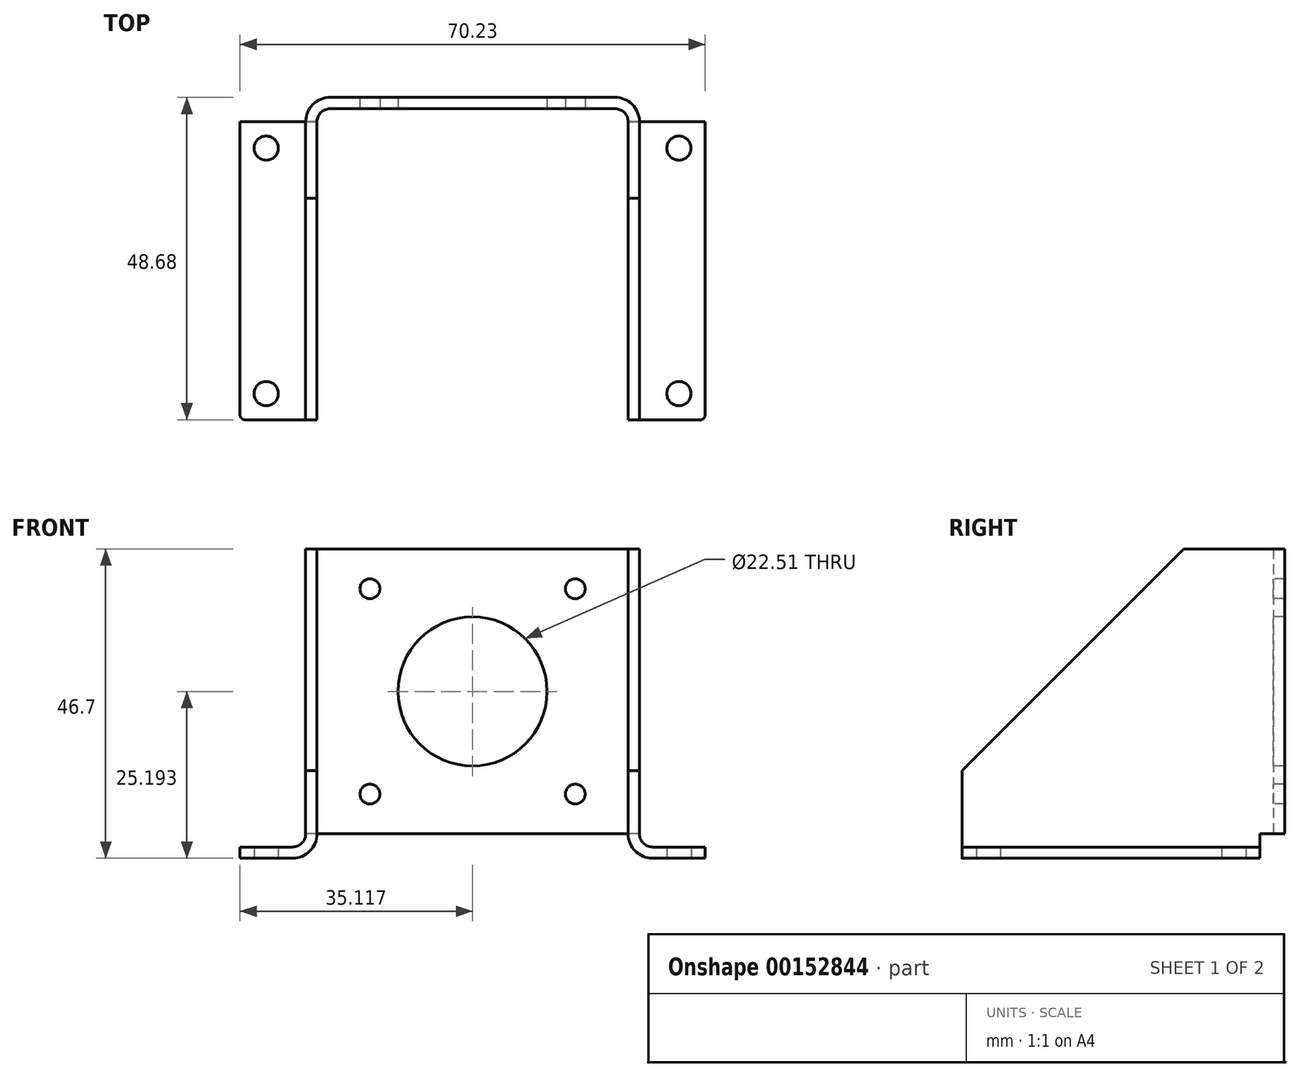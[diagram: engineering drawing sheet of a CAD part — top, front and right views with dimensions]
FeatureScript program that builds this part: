
annotation { "Feature Type Name" : "Feature", "Feature Type Description" : "" }
export const myFeature = defineFeature(function(context is Context, id is Id, definition is map)
    precondition{}
    {
        {
            var Q0;
            Q0=qCreatedBy(makeId("Top.planeOp"),FACE);
            var sketch = newSketch(context, id + "F0", { "sketchPlane" : qUnion([Q0])});
            skLineSegment(sketch, "E0.bottom", {"start": v(0, 0) * mm, "end": v(-1.7, 0) * mm});
            skLineSegment(sketch, "E1.left", {"start": v(0, 0) * mm, "end": v(0, 46.97) * mm});
            skLineSegment(sketch, "E1.right", {"start": v(-1.7, 0) * mm, "end": v(-1.7, 48.68) * mm});
            skLineSegment(sketch, "E2.bottom", {"start": v(0, 46.97) * mm, "end": v(46.97, 46.97) * mm});
            skLineSegment(sketch, "E2.top", {"start": v(-1.7, 48.68) * mm, "end": v(48.68, 48.68) * mm});
            skLineSegment(sketch, "E3.top", {"start": v(46.97, 0) * mm, "end": v(48.68, 0) * mm});
            skLineSegment(sketch, "E3.left", {"start": v(46.97, 46.97) * mm, "end": v(46.97, 0) * mm});
            skLineSegment(sketch, "E3.right", {"start": v(48.68, 48.68) * mm, "end": v(48.68, 0) * mm});
            skLineSegment(sketch, "E4", {"start": v(0, 46.97) * mm, "end": v(-1.7, 46.97) * mm, "construction": true});
            skLineSegment(sketch, "E5", {"start": v(0, 46.97) * mm, "end": v(0, 48.68) * mm, "construction": true});
            skLineSegment(sketch, "E6", {"start": v(46.97, 46.97) * mm, "end": v(48.68, 46.97) * mm, "construction": true});
            skLineSegment(sketch, "E7", {"start": v(46.97, 46.97) * mm, "end": v(46.97, 48.68) * mm, "construction": true});
            skSolve(sketch);
        }
        {
            var Q0;
            Q0=qSketchRegion(id+"F0",true);
            extrude(context, id + "F1", {"entities" : qUnion([Q0]), "depth" : 43 * mm});
        }
        {
            var Q0;
            Q0=makeQuery(id+"F1.opExtrude","SWEPT_FACE",FACE,{"disambiguationData":[OSD([sQuery(id+"F0.wireOp",EDGE,"E2.bottom")])]});
            cPlane(context, id + "F2", {"entities" : qUnion([Q0]), "cplaneType" : CPlaneType.OFFSET, "offset" : 1.98 * mm, "width" : 152.4 * mm, "height" : 152.4 * mm});
        }
        {
            var Q0;
            Q0=makeQuery(id+"F1.opExtrude","SWEPT_FACE",FACE,{"disambiguationData":[OSD([sQuery(id+"F0.wireOp",EDGE,"E3.top")])]});
            var sketch = newSketch(context, id + "F3", { "sketchPlane" : qUnion([Q0])});
            skLineSegment(sketch, "E8.bottom", {"start": v(46.97, 0) * mm, "end": v(48.68, 0) * mm});
            skLineSegment(sketch, "E8.left", {"start": v(46.97, 0) * mm, "end": v(46.97, -3.7) * mm});
            skLineSegment(sketch, "E8.right", {"start": v(48.68, 0) * mm, "end": v(48.68, -1.98) * mm});
            skLineSegment(sketch, "E9.bottom", {"start": v(48.68, -1.98) * mm, "end": v(58.6, -1.98) * mm});
            skLineSegment(sketch, "E9.top", {"start": v(46.97, -3.7) * mm, "end": v(58.6, -3.7) * mm});
            skLineSegment(sketch, "E9.right", {"start": v(58.6, -1.98) * mm, "end": v(58.6, -3.7) * mm});
            skLineSegment(sketch, "E10.bottom", {"start": v(-1.7, 0) * mm, "end": v(0, 0) * mm});
            skLineSegment(sketch, "E10.left", {"start": v(-1.7, 0) * mm, "end": v(-1.7, -1.98) * mm});
            skLineSegment(sketch, "E10.right", {"start": v(0, 0) * mm, "end": v(0, -3.7) * mm});
            skLineSegment(sketch, "E11.bottom", {"start": v(-1.7, -1.98) * mm, "end": v(-11.63, -1.98) * mm});
            skLineSegment(sketch, "E11.top", {"start": v(0, -3.7) * mm, "end": v(-11.63, -3.7) * mm});
            skLineSegment(sketch, "E11.right", {"start": v(-11.63, -1.98) * mm, "end": v(-11.63, -3.7) * mm});
            skSolve(sketch);
        }
        {
            var Q0;
            Q0=makeQuery(id+"F3.imprint","IMPRINT",FACE,{"disambiguationData":[TD([[makeQuery(id+"F3.imprint","IMPRINT",EDGE,{"derivedFrom":sQuery(id+"F3.wireOp",EDGE,"E8.bottom")}),-1.0]])]});
            var Q1;
            Q1=makeQuery(id+"F3.imprint","IMPRINT",FACE,{"disambiguationData":[TD([[makeQuery(id+"F3.imprint","IMPRINT",EDGE,{"derivedFrom":sQuery(id+"F3.wireOp",EDGE,"E10.bottom")}),-1.0]])]});
            var Q2;
            Q2=qCreatedBy(id+"F2.planeOp",FACE);
            extrude(context, id + "F4", {"entities" : qUnion([Q0, Q1]), "operationType" : NewBodyOperationType.ADD, "endBound" : BoundingType.UP_TO_SURFACE, "oppositeDirection" : true, "endBoundEntityFace" : qUnion([Q2]), "depth" : 25.4 * mm});
        }
        {
            var Q0;
            Q0=makeQuery(id+"F1.opExtrude","SWEPT_EDGE",EDGE,{"disambiguationData":[OSD([sQuery(id+"F0.wireOp",EDGE,"E1.left"),sQuery(id+"F0.wireOp",EDGE,"E2.bottom")])]});
            var Q1;
            Q1=makeQuery(id+"F1.opExtrude","SWEPT_EDGE",EDGE,{"disambiguationData":[OSD([sQuery(id+"F0.wireOp",EDGE,"E2.bottom"),sQuery(id+"F0.wireOp",EDGE,"E3.left")])]});
            var Q2;
            Q2=makeQuery(id+"F4.opExtrude","SWEPT_EDGE",EDGE,{"disambiguationData":[OSD([sQuery(id+"F3.wireOp",EDGE,"E10.left"),sQuery(id+"F3.wireOp",EDGE,"E11.bottom")])]});
            var Q3;
            Q3=makeQuery(id+"F4.opExtrude","SWEPT_EDGE",EDGE,{"disambiguationData":[OSD([sQuery(id+"F3.wireOp",EDGE,"E8.right"),sQuery(id+"F3.wireOp",EDGE,"E9.bottom")])]});
            fillet(context, id + "F5", {"entities" : qUnion([Q0, Q1, Q2, Q3]), "radius" : 1.98 * mm, "tangentPropagation" : true, "allowEdgeOverflow" : false});
        }
        {
            var Q0;
            Q0=makeQuery(id+"F1.opExtrude","SWEPT_EDGE",EDGE,{"disambiguationData":[OSD([sQuery(id+"F0.wireOp",EDGE,"E2.top"),sQuery(id+"F0.wireOp",EDGE,"E3.right")])]});
            var Q1;
            Q1=makeQuery(id+"F1.opExtrude","SWEPT_EDGE",EDGE,{"disambiguationData":[OSD([sQuery(id+"F0.wireOp",EDGE,"E1.right"),sQuery(id+"F0.wireOp",EDGE,"E2.top")])]});
            var Q2;
            Q2=makeQuery(id+"F4.opExtrude","SWEPT_EDGE",EDGE,{"disambiguationData":[OSD([sQuery(id+"F3.wireOp",EDGE,"E10.right"),sQuery(id+"F3.wireOp",EDGE,"E11.top")])]});
            var Q3;
            Q3=makeQuery(id+"F4.opExtrude","SWEPT_EDGE",EDGE,{"disambiguationData":[OSD([sQuery(id+"F3.wireOp",EDGE,"E8.left"),sQuery(id+"F3.wireOp",EDGE,"E9.top")])]});
            fillet(context, id + "F6", {"entities" : qUnion([Q0, Q1, Q2, Q3]), "radius" : 3.7 * mm, "tangentPropagation" : true, "allowEdgeOverflow" : false});
        }
        {
            var Q0;
            Q0=makeQuery(id+"F1.opExtrude","CAP_EDGE",EDGE,{"disambiguationData":[OSD([sQuery(id+"F0.wireOp",EDGE,"E0.bottom")])],"isStart":false});
            var Q1;
            Q1=makeQuery(id+"F1.opExtrude","CAP_EDGE",EDGE,{"disambiguationData":[OSD([sQuery(id+"F0.wireOp",EDGE,"E3.top")])],"isStart":false});
            chamfer(context, id + "F7", {"entities" : qUnion([Q0, Q1]), "width" : 33.48 * mm, "tangentPropagation" : true});
        }
        {
            var Q0;
            Q0=makeQuery(id+"F1.opExtrude","SWEPT_FACE",FACE,{"disambiguationData":[OSD([sQuery(id+"F0.wireOp",EDGE,"E2.bottom")])]});
            var sketch = newSketch(context, id + "F8", { "sketchPlane" : qUnion([Q0])});
            skLineSegment(sketch, "E12", {"start": v(23.49, 43) * mm, "end": v(23.49, 0) * mm, "construction": true});
            skLineSegment(sketch, "E13.bottom", {"start": v(38.99, 37) * mm, "end": v(7.99, 37) * mm, "construction": true});
            skLineSegment(sketch, "E13.top", {"start": v(38.99, 6) * mm, "end": v(7.99, 6) * mm, "construction": true});
            skLineSegment(sketch, "E13.left", {"start": v(38.99, 37) * mm, "end": v(38.99, 6) * mm, "construction": true});
            skLineSegment(sketch, "E13.right", {"start": v(7.99, 37) * mm, "end": v(7.99, 6) * mm, "construction": true});
            skPoint(sketch, "E13.middle", {"position": v(23.49, 21.5) * mm});
            skCircle(sketch, "E14", {"center": v(23.49, 21.5) * mm, "radius": 11.25 * mm});
            skCircle(sketch, "E15", {"center": v(38.99, 37) * mm, "radius": 1.5 * mm});
            skCircle(sketch, "E16", {"center": v(38.99, 6) * mm, "radius": 1.5 * mm});
            skCircle(sketch, "E17", {"center": v(7.99, 6) * mm, "radius": 1.5 * mm});
            skCircle(sketch, "E18", {"center": v(7.99, 37) * mm, "radius": 1.5 * mm});
            skSolve(sketch);
        }
        {
            var Q0;
            Q0 = qSketchRegion(id + "F8", true);
            var Q1;
            Q1=makeQuery(id+"F1.opExtrude","SWEPT_FACE",FACE,{"disambiguationData":[OSD([sQuery(id+"F0.wireOp",EDGE,"E2.top")])]});
            extrude(context, id + "F9", {"entities" : qUnion([Q0]), "operationType" : NewBodyOperationType.REMOVE, "endBound" : BoundingType.UP_TO_SURFACE, "oppositeDirection" : true, "endBoundEntityFace" : qUnion([Q1]), "depth" : 25.4 * mm});
        }
        {
            var Q0;
            Q0=makeQuery(id+"F4.opExtrude","SWEPT_FACE",FACE,{"disambiguationData":[OSD([sQuery(id+"F3.wireOp",EDGE,"E11.top")])]});
            var sketch = newSketch(context, id + "F10", { "sketchPlane" : qUnion([Q0])});
            skLineSegment(sketch, "E19", {"start": v(-3.7, -22.5) * mm, "end": v(50.67, -22.5) * mm, "construction": true});
            skLineSegment(sketch, "E20.bottom", {"start": v(-11.63, -44.99) * mm, "end": v(-7.66, -44.99) * mm, "construction": true});
            skLineSegment(sketch, "E20.top", {"start": v(-11.63, -41.02) * mm, "end": v(-7.66, -41.02) * mm, "construction": true});
            skLineSegment(sketch, "E20.left", {"start": v(-11.63, -44.99) * mm, "end": v(-11.63, -41.02) * mm, "construction": true});
            skLineSegment(sketch, "E20.right", {"start": v(-7.66, -44.99) * mm, "end": v(-7.66, -41.02) * mm, "construction": true});
            skLineSegment(sketch, "E21.bottom", {"start": v(-7.66, -41.02) * mm, "end": v(54.64, -41.02) * mm, "construction": true});
            skLineSegment(sketch, "E21.top", {"start": v(-7.66, -3.97) * mm, "end": v(54.64, -3.97) * mm, "construction": true});
            skLineSegment(sketch, "E21.left", {"start": v(-7.66, -41.02) * mm, "end": v(-7.66, -3.97) * mm, "construction": true});
            skLineSegment(sketch, "E21.right", {"start": v(54.64, -41.02) * mm, "end": v(54.64, -3.97) * mm, "construction": true});
            skPoint(sketch, "E21.middle", {"position": v(23.49, -22.5) * mm});
            skCircle(sketch, "E22", {"center": v(54.64, -41.02) * mm, "radius": 1.83 * mm});
            skCircle(sketch, "E23", {"center": v(-7.66, -41.02) * mm, "radius": 1.83 * mm});
            skCircle(sketch, "E24", {"center": v(-7.66, -3.97) * mm, "radius": 1.83 * mm});
            skCircle(sketch, "E25", {"center": v(54.64, -3.97) * mm, "radius": 1.83 * mm});
            skSolve(sketch);
        }
        {
            var Q0;
            Q0 = qSketchRegion(id + "F10", true);
            var Q1;
            Q1=makeQuery(id+"F4.opExtrude","SWEPT_FACE",FACE,{"disambiguationData":[OSD([sQuery(id+"F3.wireOp",EDGE,"E11.bottom")])]});
            extrude(context, id + "F11", {"entities" : qUnion([Q0]), "operationType" : NewBodyOperationType.REMOVE, "endBound" : BoundingType.UP_TO_SURFACE, "oppositeDirection" : true, "endBoundEntityFace" : qUnion([Q1]), "depth" : 25.4 * mm});
        }
        {
            var Q0;
            Q0=makeQuery(id+"F4.opExtrude","TWEAK_EDGE",EDGE,{"derivedFrom":[dummyQuery(id+"F2.planeOp",FACE),makeQuery(id+"F3.imprint","IMPRINT",EDGE,{"derivedFrom":sQuery(id+"F3.wireOp",EDGE,"E9.right")})]});
            var Q1;
            Q1=makeQuery(id+"F4.opExtrude","CAP_EDGE",EDGE,{"disambiguationData":[OSD([sQuery(id+"F3.wireOp",EDGE,"E9.right")])],"isStart":true});
            var Q2;
            Q2=makeQuery(id+"F4.opExtrude","CAP_EDGE",EDGE,{"disambiguationData":[OSD([sQuery(id+"F3.wireOp",EDGE,"E11.right")])],"isStart":true});
            var Q3;
            Q3=makeQuery(id+"F4.opExtrude","TWEAK_EDGE",EDGE,{"derivedFrom":[dummyQuery(id+"F2.planeOp",FACE),makeQuery(id+"F3.imprint","IMPRINT",EDGE,{"derivedFrom":sQuery(id+"F3.wireOp",EDGE,"E11.right")})]});
            fillet(context, id + "F12", {"entities" : qUnion([Q0, Q1, Q2, Q3]), "radius" : 0.76 * mm, "tangentPropagation" : true, "allowEdgeOverflow" : false});
        }
    });
